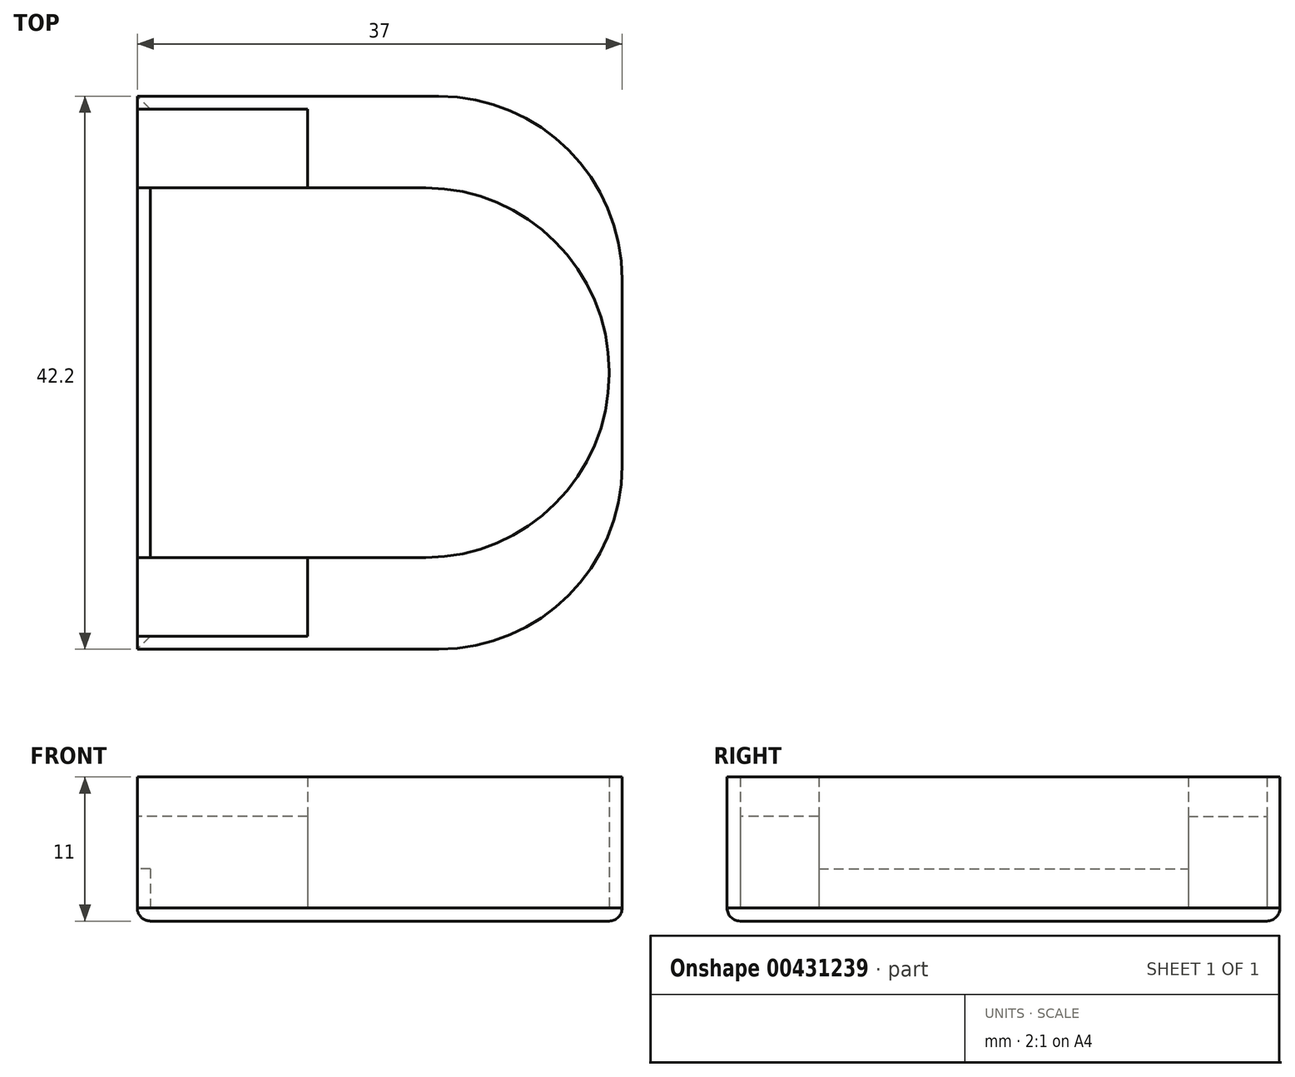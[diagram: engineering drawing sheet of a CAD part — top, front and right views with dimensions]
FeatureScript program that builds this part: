
annotation { "Feature Type Name" : "Feature", "Feature Type Description" : "" }
export const myFeature = defineFeature(function(context is Context, id is Id, definition is map)
    precondition{}
    {
        {
            var Q0;
            Q0=qCreatedBy(makeId("Top.planeOp"),FACE);
            var sketch = newSketch(context, id + "F0", { "sketchPlane" : qUnion([Q0])});
            skLineSegment(sketch, "E0.bottom", {"start": v(17.5, -20.1) * mm, "end": v(-17.5, -20.1) * mm});
            skLineSegment(sketch, "E0.top", {"start": v(17.5, 20.1) * mm, "end": v(-17.5, 20.1) * mm});
            skLineSegment(sketch, "E0.left", {"start": v(17.5, -20.1) * mm, "end": v(17.5, 20.1) * mm});
            skLineSegment(sketch, "E0.right", {"start": v(-17.5, -20.1) * mm, "end": v(-17.5, 20.1) * mm});
            skPoint(sketch, "E0.middle", {"position": v(0, 0) * mm});
            skLineSegment(sketch, "E1.0", {"start": v(18.5, 21.1) * mm, "end": v(-18.5, 21.1) * mm});
            skLineSegment(sketch, "E1.1", {"start": v(18.5, -21.1) * mm, "end": v(18.5, 21.1) * mm});
            skLineSegment(sketch, "E1.2", {"start": v(18.5, -21.1) * mm, "end": v(-18.5, -21.1) * mm});
            skLineSegment(sketch, "E1.3", {"start": v(-18.5, -21.1) * mm, "end": v(-18.5, 21.1) * mm});
            skLineSegment(sketch, "E2", {"start": v(-17.5, 20.1) * mm, "end": v(-18.5, 20.1) * mm});
            skLineSegment(sketch, "E3", {"start": v(-17.5, -20.1) * mm, "end": v(-18.5, -20.1) * mm});
            skLineSegment(sketch, "E4", {"start": v(-17.5, 14.1) * mm, "end": v(-5.5, 14.1) * mm});
            skLineSegment(sketch, "E5", {"start": v(-5.5, 14.1) * mm, "end": v(-5.5, 20.1) * mm});
            skLineSegment(sketch, "E6", {"start": v(-17.5, -14.1) * mm, "end": v(-5.5, -14.1) * mm});
            skLineSegment(sketch, "E7", {"start": v(-5.5, -14.1) * mm, "end": v(-5.5, -20.1) * mm});
            skLineSegment(sketch, "E8", {"start": v(-5.5, 14.1) * mm, "end": v(17.5, 14.1) * mm});
            skLineSegment(sketch, "E9", {"start": v(-5.5, -14.1) * mm, "end": v(17.5, -14.1) * mm});
            skLineSegment(sketch, "E10", {"start": v(-17.5, 14.1) * mm, "end": v(-18.5, 14.1) * mm});
            skLineSegment(sketch, "E11", {"start": v(-17.5, -14.1) * mm, "end": v(-18.5, -14.1) * mm});
            skSolve(sketch);
        }
        {
            var Q0;
            {var subQ0=sQuery(id+"F0.wireOp",EDGE,"E10");Q0=makeQuery(id+"F0.imprint","IMPRINT",FACE,{"disambiguationData":[TD([[makeQuery(id+"F0.imprint","IMPRINT",EDGE,{"derivedFrom":subQ0}),1.0]])]});}
            extrude(context, id + "F1", {"entities" : qUnion([Q0]), "depth" : 3 * mm});
        }
        {
            var Q0;
            {var subQ0=sQuery(id+"F0.wireOp",EDGE,"E2");Q0=makeQuery(id+"F0.imprint","IMPRINT",FACE,{"disambiguationData":[TD([[makeQuery(id+"F0.imprint","IMPRINT",EDGE,{"derivedFrom":subQ0}),1.0]])]});}
            var Q1;
            {var subQ0=sQuery(id+"F0.wireOp",EDGE,"E3");Q1=makeQuery(id+"F0.imprint","IMPRINT",FACE,{"disambiguationData":[TD([[makeQuery(id+"F0.imprint","IMPRINT",EDGE,{"derivedFrom":subQ0}),-1.0]])]});}
            var Q2;
            {var subQ4=sQuery(id+"F0.wireOp",EDGE,"E6");Q2=makeQuery(id+"F0.imprint","IMPRINT",FACE,{"disambiguationData":[TD([[makeQuery(id+"F0.imprint","IMPRINT",EDGE,{"derivedFrom":subQ4}),-1.0]])]});}
            var Q3;
            {var subQ4=sQuery(id+"F0.wireOp",EDGE,"E4");Q3=makeQuery(id+"F0.imprint","IMPRINT",FACE,{"disambiguationData":[TD([[makeQuery(id+"F0.imprint","IMPRINT",EDGE,{"derivedFrom":subQ4}),1.0]])]});}
            extrude(context, id + "F2", {"entities" : qUnion([Q0, Q1, Q2, Q3]), "depth" : 7 * mm});
        }
        {
            var Q0;
            {var subQ0=sQuery(id+"F0.wireOp",EDGE,"E1.0");Q0=makeQuery(id+"F0.imprint","IMPRINT",FACE,{"disambiguationData":[TD([[makeQuery(id+"F0.imprint","IMPRINT",EDGE,{"derivedFrom":subQ0}),1.0]])]});}
            var Q1;
            {var subQ3=sQuery(id+"F0.wireOp",EDGE,"E5");Q1=makeQuery(id+"F0.imprint","IMPRINT",FACE,{"disambiguationData":[TD([[makeQuery(id+"F0.imprint","IMPRINT",EDGE,{"derivedFrom":subQ3}),-1.0]])]});}
            var Q2;
            {var subQ3=sQuery(id+"F0.wireOp",EDGE,"E7");Q2=makeQuery(id+"F0.imprint","IMPRINT",FACE,{"disambiguationData":[TD([[makeQuery(id+"F0.imprint","IMPRINT",EDGE,{"derivedFrom":subQ3}),1.0]])]});}
            extrude(context, id + "F3", {"entities" : qUnion([Q0, Q1, Q2]), "depth" : 10 * mm});
        }
        {
            var Q0;
            {var subQ1=sQuery(id+"F0.wireOp",EDGE,"E4");Q0=makeQuery(id+"F0.imprint","IMPRINT",FACE,{"disambiguationData":[TD([[makeQuery(id+"F0.imprint","IMPRINT",EDGE,{"derivedFrom":subQ1}),-1.0]])]});}
            var Q1;
            {var subQ0=sQuery(id+"F0.wireOp",EDGE,"E2");Q1=makeQuery(id+"F0.imprint","IMPRINT",FACE,{"disambiguationData":[TD([[makeQuery(id+"F0.imprint","IMPRINT",EDGE,{"derivedFrom":subQ0}),1.0]])]});}
            var Q2;
            {var subQ0=sQuery(id+"F0.wireOp",EDGE,"E1.0");Q2=makeQuery(id+"F0.imprint","IMPRINT",FACE,{"disambiguationData":[TD([[makeQuery(id+"F0.imprint","IMPRINT",EDGE,{"derivedFrom":subQ0}),1.0]])]});}
            var Q3;
            {var subQ4=sQuery(id+"F0.wireOp",EDGE,"E4");Q3=makeQuery(id+"F0.imprint","IMPRINT",FACE,{"disambiguationData":[TD([[makeQuery(id+"F0.imprint","IMPRINT",EDGE,{"derivedFrom":subQ4}),1.0]])]});}
            var Q4;
            {var subQ3=sQuery(id+"F0.wireOp",EDGE,"E5");Q4=makeQuery(id+"F0.imprint","IMPRINT",FACE,{"disambiguationData":[TD([[makeQuery(id+"F0.imprint","IMPRINT",EDGE,{"derivedFrom":subQ3}),-1.0]])]});}
            var Q5;
            {var subQ0=sQuery(id+"F0.wireOp",EDGE,"E10");Q5=makeQuery(id+"F0.imprint","IMPRINT",FACE,{"disambiguationData":[TD([[makeQuery(id+"F0.imprint","IMPRINT",EDGE,{"derivedFrom":subQ0}),1.0]])]});}
            var Q6;
            {var subQ0=sQuery(id+"F0.wireOp",EDGE,"E3");Q6=makeQuery(id+"F0.imprint","IMPRINT",FACE,{"disambiguationData":[TD([[makeQuery(id+"F0.imprint","IMPRINT",EDGE,{"derivedFrom":subQ0}),-1.0]])]});}
            var Q7;
            {var subQ4=sQuery(id+"F0.wireOp",EDGE,"E6");Q7=makeQuery(id+"F0.imprint","IMPRINT",FACE,{"disambiguationData":[TD([[makeQuery(id+"F0.imprint","IMPRINT",EDGE,{"derivedFrom":subQ4}),-1.0]])]});}
            var Q8;
            {var subQ3=sQuery(id+"F0.wireOp",EDGE,"E7");Q8=makeQuery(id+"F0.imprint","IMPRINT",FACE,{"disambiguationData":[TD([[makeQuery(id+"F0.imprint","IMPRINT",EDGE,{"derivedFrom":subQ3}),1.0]])]});}
            extrude(context, id + "F4", {"entities" : qUnion([Q0, Q1, Q2, Q3, Q4, Q5, Q6, Q7, Q8]), "oppositeDirection" : true, "depth" : 1 * mm});
        }
        {
            var Q0;
            Q0=makeQuery(id+"F3.opExtrude","SWEPT_EDGE",EDGE,{"disambiguationData":[OSD([sQuery(id+"F0.wireOp",EDGE,"E0.left"),sQuery(id+"F0.wireOp",EDGE,"E8")])]});
            var Q1;
            Q1=makeQuery(id+"F3.opExtrude","SWEPT_EDGE",EDGE,{"disambiguationData":[OSD([sQuery(id+"F0.wireOp",EDGE,"E0.left"),sQuery(id+"F0.wireOp",EDGE,"E9")])]});
            var Q2;
            Q2=makeQuery(id+"F3.opExtrude","SWEPT_EDGE",EDGE,{"disambiguationData":[OSD([sQuery(id+"F0.wireOp",EDGE,"E1.0"),sQuery(id+"F0.wireOp",EDGE,"E1.1")])]});
            var Q3;
            Q3=makeQuery(id+"F4.opExtrude","SWEPT_EDGE",EDGE,{"disambiguationData":[OSD([sQuery(id+"F0.wireOp",EDGE,"E1.0"),sQuery(id+"F0.wireOp",EDGE,"E1.1")])]});
            var Q4;
            Q4=makeQuery(id+"F3.opExtrude","SWEPT_EDGE",EDGE,{"disambiguationData":[OSD([sQuery(id+"F0.wireOp",EDGE,"E1.1"),sQuery(id+"F0.wireOp",EDGE,"E1.2")])]});
            var Q5;
            Q5=makeQuery(id+"F4.opExtrude","SWEPT_EDGE",EDGE,{"disambiguationData":[OSD([sQuery(id+"F0.wireOp",EDGE,"E1.1"),sQuery(id+"F0.wireOp",EDGE,"E1.2")])]});
            fillet(context, id + "F5", {"entities" : qUnion([Q0, Q1, Q2, Q3, Q4, Q5]), "radius" : 14 * mm, "tangentPropagation" : true, "allowEdgeOverflow" : false});
        }
        {
            var Q0;
            Q0=makeQuery(id+"F4.opExtrude","CAP_EDGE",EDGE,{"disambiguationData":[OSD([sQuery(id+"F0.wireOp",EDGE,"E1.2")])],"isStart":false});
            var Q1;
            Q1=makeQuery(id+"F4.opExtrude","CAP_EDGE",EDGE,{"disambiguationData":[OSD([sQuery(id+"F0.wireOp",EDGE,"E1.3")])],"isStart":false});
            fillet(context, id + "F6", {"entities" : qUnion([Q0, Q1]), "radius" : 1 * mm, "tangentPropagation" : true, "allowEdgeOverflow" : false});
        }
    });
